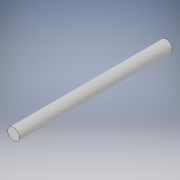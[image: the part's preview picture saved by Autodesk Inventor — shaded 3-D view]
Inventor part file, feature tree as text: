
AUTODESK INVENTOR PART (.ipt)
format: ipt  version: 2019 (Build 230136000, 136)  size: 91,136 bytes
history: native  units: mm
features: extrude x1, sketch x1
ambient origin geometry x8: Origin, YZ Plane, XZ Plane, XY Plane, X Axis, Y Axis, Z Axis, Center Point
bodies: Solid1 (feature_tree)
feature tree (2):
  extrude  "Extrusion1"  Depth=92.0mm TaperAngle=0.0deg
  sketch  "Sketch1"  dims[d0=7.0mm d1=92.0mm d2=0.0mm]
